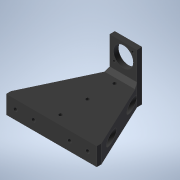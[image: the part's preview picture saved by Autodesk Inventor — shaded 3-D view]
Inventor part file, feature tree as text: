
AUTODESK INVENTOR PART (.ipt)
format: ipt  version: 2021 (Build 250183000, 183)  size: 187,904 bytes
history: native  units: mm
features: extrude x6, sketch x4, chamfer x1, projected_geometry x1
ambient origin geometry x8: Origin, YZ Plane, XZ Plane, XY Plane, X Axis, Y Axis, Z Axis, Center Point
bodies: Solid1 (feature_tree)
feature tree (12):
  extrude  "Extrusion1"  Depth=100.0mm
  sketch  "Sketch2"  dims[d2=5.5mm d3=85.0mm]
  extrude  "Extrusion2"  Depth=85.0mm
  extrude  "Extrusion3"  Depth=30.0mm
  extrude  "Extrusion4"  Depth=10.0mm
  extrude  "Extrusion5"  Depth=10.0mm
  chamfer  "Chamfer1"  Distance=20.0mm
  extrude  "Extrusion6"  Depth=20.0mm
  sketch  "Sketch1"  dims[d0=5.0mm d1=100.0mm]
  projected_geometry  "Projected Loop1"
  sketch  "Sketch3"  dims[d4=42.5mm d5=30.0mm]
  sketch  "Sketch4"  dims[d6=20.0mm d7=0.0mm d8=10.0mm d9=10.0mm d10=20.0mm d11=20.0mm d12=10.0mm d13=4.3mm d14=82.0mm d15=0.0mm d16=0.0mm d17=0.0mm d18=5.5mm d19=0.0mm d20=21.0mm d21=22.0mm d22=35.0mm d23=0.0mm d24=0.0mm d27=14.0mm d28=2.8mm d29=14.0mm d30=4.0mm d31=2.0mm d32=45.0deg d33=4.2mm d34=10.0mm d35=30.0mm d36=30.0mm d37=10.0mm d38=0.0mm]
